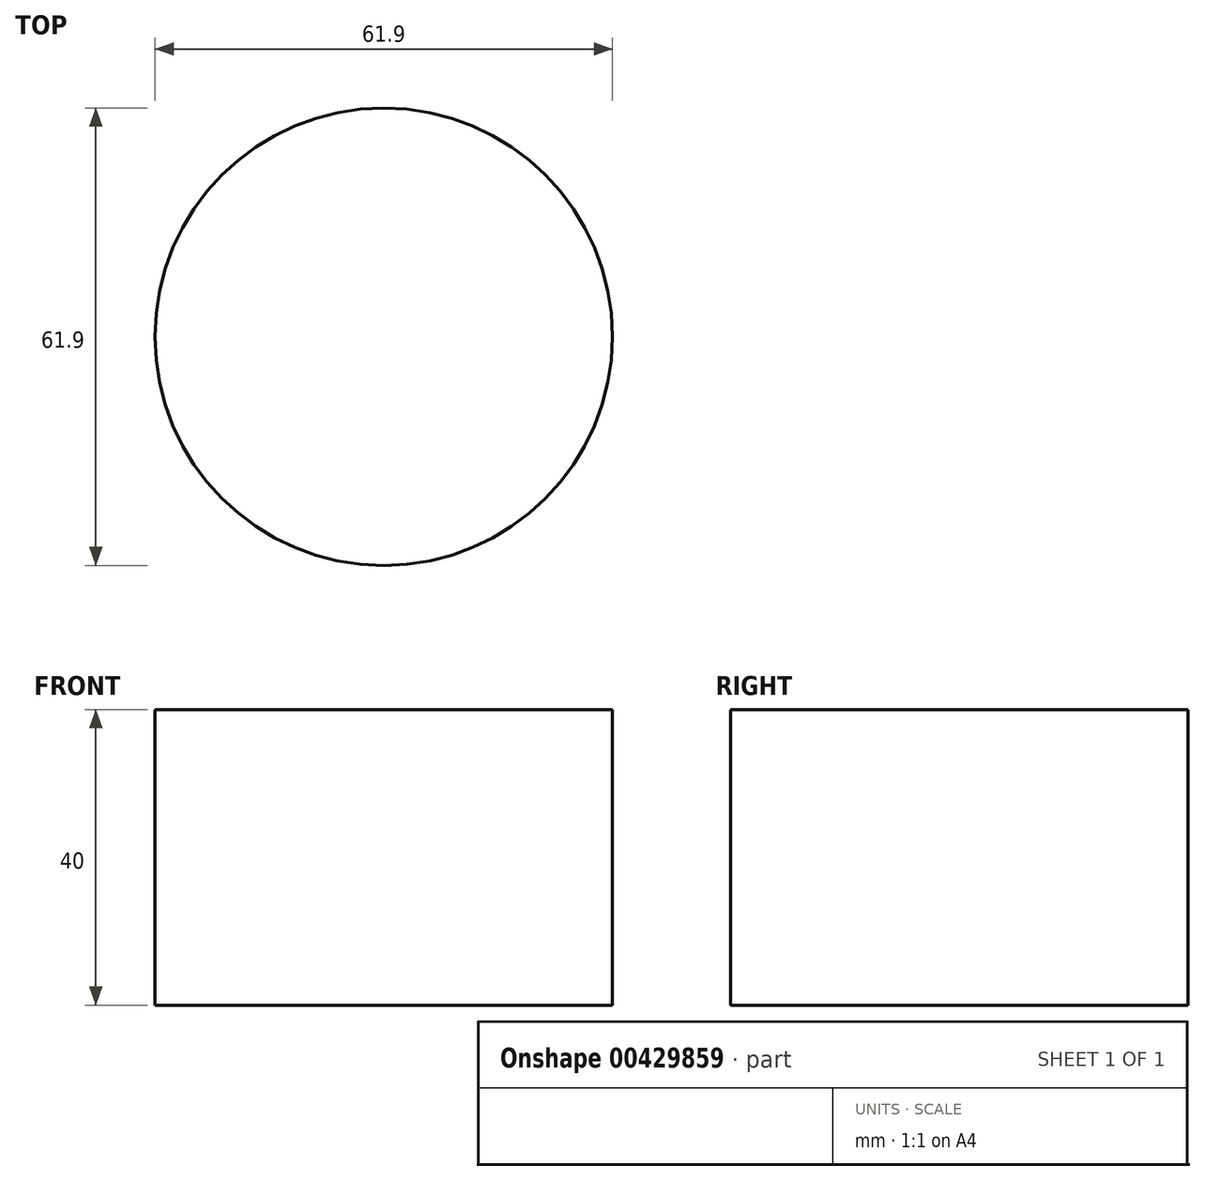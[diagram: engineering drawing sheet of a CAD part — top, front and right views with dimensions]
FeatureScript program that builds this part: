
annotation { "Feature Type Name" : "Feature", "Feature Type Description" : "" }
export const myFeature = defineFeature(function(context is Context, id is Id, definition is map)
    precondition{}
    {
        {
            var Q0;
            Q0=qCreatedBy(makeId("Top.planeOp"),FACE);
            var sketch = newSketch(context, id + "F0", { "sketchPlane" : qUnion([Q0])});
            skCircle(sketch, "E0", {"center": v(0, 0) * mm, "radius": 30.95 * mm});
            skSolve(sketch);
        }
        {
            var Q0;
            Q0 = qSketchRegion(id + "F0", true);
            extrude(context, id + "F1", {"entities" : qUnion([Q0]), "depth" : 40 * mm});
        }
    });
